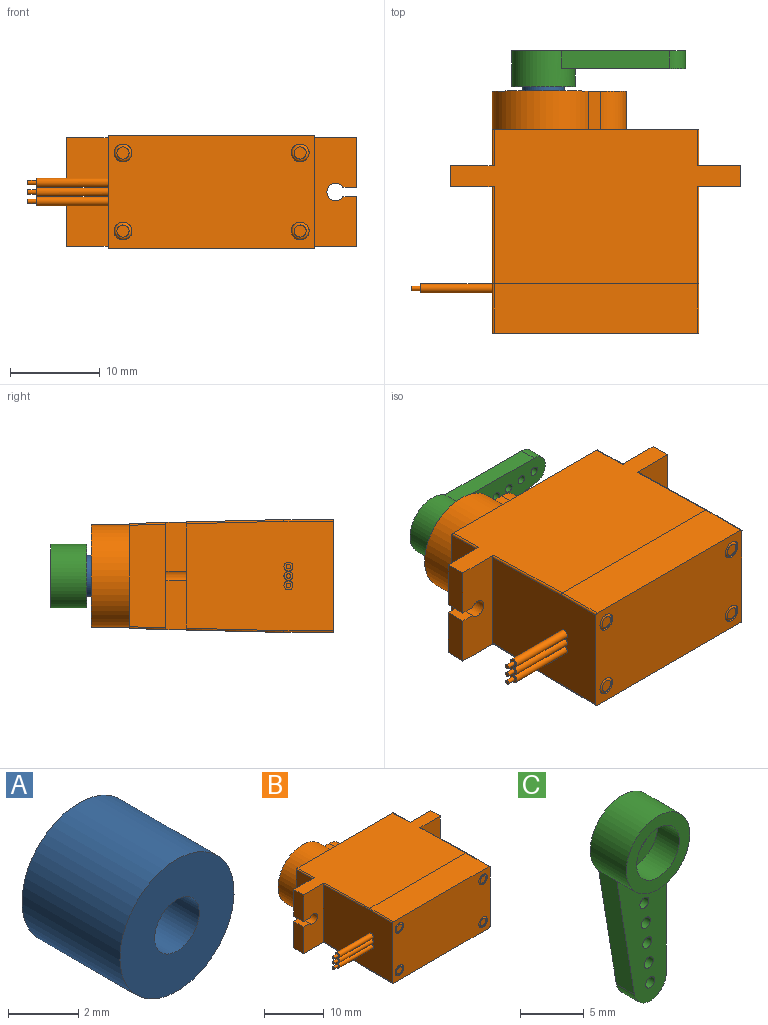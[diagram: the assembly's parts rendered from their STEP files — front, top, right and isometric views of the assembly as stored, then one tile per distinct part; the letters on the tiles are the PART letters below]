
ASSEMBLY  parts=3 mates=2
PART A: 4 faces, bbox 4.6x4x4.6 mm
  f0: cylinder r=2.3mm len=4.6mm, axis (0,1,0), area 57.1mm2, adj f1,f3
  f1: plane 4.6x4.6mm, normal (0,-1,0), area 14.1mm2, adj f0,f2
  f2: cylinder r=0.9mm len=3.95mm, axis (0,1,0), area 22.3mm2, adj f1,f3
  f3: plane 4.6x4.6mm, normal (0,1,0), area 14.1mm2, adj f0,f2
PART B: 75 faces, bbox 36.7x27x12.6 mm
  f0: plane 1x1mm, normal (-1,0,0), area 0.6mm2, adj f50,f55
  f1: plane 1x1mm, normal (-1,0,0), area 0.6mm2, adj f49,f53
  f2: plane 1x1mm, normal (-1,0,0), area 0.6mm2, adj f48,f51
  f3: plane 16.34x12.19mm, normal (-1,0,0), area 193.9mm2, adj f9,f17,f48,f49,f50,f61,f62,f63
  f4: plane 12.04x4.84mm, normal (0,-1,0), area 51.4mm2, adj f5,f13,f14,f24,f25,f29,f30,f31
  f5: plane 5.48x2.32mm, normal (1,0,0), area 12.6mm2, adj f4,f6,f25,f30
  f6: plane 11.93x4.84mm, normal (0,1,0), area 50.8mm2, adj f5,f14,f15,f24,f25,f29,f30,f31
  f7: plane 11.93x4.84mm, normal (0,1,0), area 50.8mm2, adj f8,f11,f12,f24,f25,f26,f27,f28
  f8: plane 5.48x2.32mm, normal (-1,0,0), area 12.6mm2, adj f7,f9,f24,f27
  f9: plane 12.04x4.84mm, normal (0,-1,0), area 51.4mm2, adj f3,f8,f12,f24,f25,f26,f27,f28
  f10: plane 23.03x11.72mm, normal (0,1,0), area 149mm2, adj f11,f15,f19,f20,f21,f22,f24,f25
  f11: plane 11.53x4.06mm, normal (-1,0,0), area 46.4mm2, adj f7,f10,f71,f72
  f12: plane 5.48x2.32mm, normal (-1,0,0), area 12.6mm2, adj f7,f9,f25,f28
  f13: plane 16.34x12.19mm, normal (1,0,0), area 196.2mm2, adj f4,f17,f65,f66,f67,f68
  f14: plane 5.48x2.32mm, normal (1,0,0), area 12.6mm2, adj f4,f6,f24,f31
  f15: plane 11.53x4.06mm, normal (1,0,0), area 46.4mm2, adj f6,f10,f69,f70
  f16: plane 22.63x5.5mm, normal (0,0,1), area 124.5mm2, adj f17,f25,f61,f65
  f17: plane 23.03x12.59mm, normal (0,-1,0), area 277.3mm2, adj f3,f13,f16,f18,f32,f36,f40,f44
  f18: plane 22.63x5.5mm, normal (0,0,-1), area 124.5mm2, adj f17,f24,f63,f67
  f19: cylinder r=5.72mm len=11.45mm, axis (0,-1,0), area 128.4mm2, adj f10,f20,f22,f23
  f20: plane 4.28x1.41mm, normal (0,0,1), area 6mm2, adj f10,f19,f21,f23
  f21: cylinder r=2.85mm len=5.7mm, axis (0,-1,0), area 38.3mm2, adj f10,f20,f22,f23
  f22: plane 4.28x1.41mm, normal (0,0,-1), area 6mm2, adj f10,f19,f21,f23
  f23: plane 14.95x11.45mm, normal (0,1,0), area 103.5mm2, adj f19,f20,f21,f22,f73
  f24: plane 32.31x17.22mm, normal (0,0.03,-1), area 412.3mm2, adj f4,f6,f7,f8,f9,f10,f14,f18
  f25: plane 32.31x17.22mm, normal (0,0.03,1), area 412.3mm2, adj f4,f5,f6,f7,f9,f10,f12,f16
  f26: cylinder r=0.97mm len=2.32mm, axis (0,-1,0), area 11.5mm2, adj f7,f9,f27,f28
  f27: plane 2.32x1.51mm, normal (0,0,1), area 3.5mm2, adj f7,f8,f9,f26
  f28: plane 2.32x1.51mm, normal (0,0,-1), area 3.5mm2, adj f7,f9,f12,f26
  f29: cylinder r=0.97mm len=2.32mm, axis (0,-1,0), area 11.5mm2, adj f4,f6,f30,f31
  f30: plane 2.32x1.51mm, normal (0,0,-1), area 3.5mm2, adj f4,f5,f6,f29
  f31: plane 2.32x1.51mm, normal (0,0,1), area 3.5mm2, adj f4,f6,f14,f29
  f32: cylinder r=1mm len=2mm, axis (0,-1,0), area 6.3mm2, adj f17,f33
  f33: plane 2x2mm, normal (0,-1,0), area 0.2mm2, adj f32,f34
  f34: cylinder r=0.97mm len=1.95mm, axis (0,-1,0), area 4.3mm2, adj f33,f60
  f35: plane 1.35x1.35mm, normal (0,-1,0), area 1.4mm2, adj f60
  f36: cylinder r=1mm len=2mm, axis (0,-1,0), area 6.3mm2, adj f17,f37
  f37: plane 2x2mm, normal (0,-1,0), area 0.2mm2, adj f36,f38
  f38: cylinder r=0.97mm len=1.95mm, axis (0,-1,0), area 4.3mm2, adj f37,f59
  f39: plane 1.35x1.35mm, normal (0,-1,0), area 1.4mm2, adj f59
  f40: cylinder r=1mm len=2mm, axis (0,-1,0), area 6.3mm2, adj f17,f41
  f41: plane 2x2mm, normal (0,-1,0), area 0.2mm2, adj f40,f42
  f42: cylinder r=0.97mm len=1.95mm, axis (0,-1,0), area 4.3mm2, adj f41,f57
  f43: plane 1.35x1.35mm, normal (0,-1,0), area 1.4mm2, adj f57
  f44: cylinder r=1mm len=2mm, axis (0,-1,0), area 6.3mm2, adj f17,f45
  f45: plane 2x2mm, normal (0,-1,0), area 0.2mm2, adj f44,f46
  f46: cylinder r=0.97mm len=1.95mm, axis (0,-1,0), area 4.3mm2, adj f45,f58
  f47: plane 1.35x1.35mm, normal (0,-1,0), area 1.4mm2, adj f58
  f48: cylinder r=0.5mm len=8mm, axis (1,0,0), area 25.1mm2, adj f2,f3
  f49: cylinder r=0.5mm len=8mm, axis (1,0,0), area 25.1mm2, adj f1,f3
  f50: cylinder r=0.5mm len=8mm, axis (1,0,0), area 25.1mm2, adj f0,f3
  f51: cylinder r=0.25mm len=1mm, axis (1,0,0), area 1.6mm2, adj f2,f52
  f52: plane 0.5x0.5mm, normal (-1,0,0), area 0.2mm2, adj f51
  f53: cylinder r=0.25mm len=1mm, axis (1,0,0), area 1.6mm2, adj f1,f54
  f54: plane 0.5x0.5mm, normal (-1,0,0), area 0.2mm2, adj f53
  f55: cylinder r=0.25mm len=1mm, axis (1,0,0), area 1.6mm2, adj f0,f56
  f56: plane 0.5x0.5mm, normal (-1,0,0), area 0.2mm2, adj f55
  f57: torus R=0.68mm, axis (0,1,0), area 2.6mm2, adj f42,f43
  f58: torus R=0.68mm, axis (0,1,0), area 2.6mm2, adj f46,f47
  f59: torus R=0.68mm, axis (0,1,0), area 2.6mm2, adj f38,f39
  f60: torus R=0.68mm, axis (0,1,0), area 2.6mm2, adj f34,f35
  f61: cylinder r=0.2mm len=5.5mm, axis (0,1,0), area 1.7mm2, adj f3,f16,f17,f62
  f62: cylinder r=0.2mm len=10.85mm, axis (0,1,-0.03), area 3.4mm2, adj f3,f9,f25,f61
  f63: cylinder r=0.2mm len=5.5mm, axis (0,-1,0), area 1.7mm2, adj f3,f17,f18,f64
  f64: cylinder r=0.2mm len=10.85mm, axis (0,-1,-0.03), area 3.4mm2, adj f3,f9,f24,f63
  f65: cylinder r=0.2mm len=5.5mm, axis (0,-1,0), area 1.7mm2, adj f13,f16,f17,f66
  f66: cylinder r=0.2mm len=10.85mm, axis (0,-1,0.03), area 3.4mm2, adj f4,f13,f25,f65
  f67: cylinder r=0.2mm len=5.5mm, axis (0,1,0), area 1.7mm2, adj f13,f17,f18,f68
  f68: cylinder r=0.2mm len=10.85mm, axis (0,1,0.03), area 3.4mm2, adj f4,f13,f24,f67
  f69: cylinder r=0.2mm len=4.07mm, axis (0,1,0.03), area 1.3mm2, adj f6,f10,f15,f24
  f70: cylinder r=0.2mm len=4.07mm, axis (0,-1,0.03), area 1.3mm2, adj f6,f10,f15,f25
  f71: cylinder r=0.2mm len=4.07mm, axis (0,-1,-0.03), area 1.3mm2, adj f7,f10,f11,f24
  f72: cylinder r=0.2mm len=4.07mm, axis (0,1,-0.03), area 1.3mm2, adj f7,f10,f11,f25
  f73: cylinder r=2.35mm len=4.7mm, axis (0,1,0), area 30.3mm2, adj f23,f74
  f74: plane 4.7x4.7mm, normal (0,1,0), area 17.3mm2, adj f73
PART C: 18 faces, bbox 7.1x4x19.4 mm
  f0: cylinder r=3.54mm len=7.07mm, axis (0,1,0), area 76.1mm2, adj f1,f7,f9,f16,f17
  f1: plane 19.35x7.07mm, normal (0,1,0), area 69.3mm2, adj f0,f2,f8,f9,f10,f11,f12,f13
  f2: cylinder r=2.48mm len=4.95mm, axis (0,1,0), area 12.4mm2, adj f1,f3
  f3: plane 4.95x4.95mm, normal (0,1,0), area 14.4mm2, adj f2,f4
  f4: cylinder r=1.25mm len=2.49mm, axis (0,1,0), area 5.9mm2, adj f3,f5
  f5: plane 4.75x4.75mm, normal (0,-1,0), area 12.9mm2, adj f4,f6
  f6: cylinder r=2.38mm len=4.75mm, axis (0,1,0), area 36.6mm2, adj f5,f7
  f7: plane 7.07x7.07mm, normal (0,-1,0), area 21.5mm2, adj f0,f6
  f8: cylinder r=0.5mm len=2mm, axis (0,-1,0), area 6.3mm2, adj f1,f16
  f9: plane 12.08x2mm, normal (1,0,0), area 24.2mm2, adj f0,f1,f10,f16
  f10: cylinder r=1.78mm len=3.54mm, axis (0,-1,0), area 10.6mm2, adj f1,f9,f16,f17
  f11: cylinder r=0.5mm len=2mm, axis (0,-1,0), area 6.3mm2, adj f1,f16
  f12: cylinder r=0.5mm len=2mm, axis (0,-1,0), area 6.3mm2, adj f1,f16
  f13: cylinder r=0.5mm len=2mm, axis (0,-1,0), area 6.3mm2, adj f1,f16
  f14: cylinder r=0.5mm len=2mm, axis (0,-1,0), area 6.3mm2, adj f1,f16
  f15: cylinder r=0.5mm len=2mm, axis (0,-1,0), area 6.3mm2, adj f1,f16
  f16: plane 13.86x5.53mm, normal (0,-1,0), area 49.3mm2, adj f0,f8,f9,f10,f11,f12,f13,f14
  f17: plane 11.92x2mm, normal (-0.99,0,-0.16), area 24.2mm2, adj f0,f1,f10,f16
PLACE A t=(4.96,32.22,4.62)mm
PLACE B t=(4.96,32.22,4.62)mm
PLACE C rot(axis=(0,-1,0),90deg) t=(3.55,32.22,6.02)mm
MATE fastened A.f0 <-> B.f19  axis (0,1,0) through (3.55,41.88,4.62)mm
MATE revolute C.f0 <-> A.f0  axis (0,-1,0) through (3.55,45.83,4.62)mm
